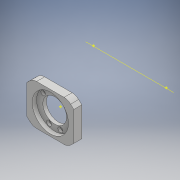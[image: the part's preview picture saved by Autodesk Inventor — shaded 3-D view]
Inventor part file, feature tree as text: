
AUTODESK INVENTOR PART (.ipt)
format: ipt  version: 2018 (Build 220112000, 112)  size: 751,616 bytes
history: native  units: mm
features: sketch x38, projected_geometry x38, extrude x32, other x10, chamfer x7, fillet x5, hole x4, reference x3, mirror x1, plane x1
ambient origin geometry x8: Origin, YZ Plane, XZ Plane, XY Plane, X Axis, Y Axis, Z Axis, Center Point
bodies: Solid1 (feature_tree)
feature tree (139):
  extrude  "Extrusion1"  Depth=45.0mm
  extrude  "Extrusion2"  Depth=2.25mm
  hole  "Hole1"  [1 undecoded]
  hole  "Hole2"  [1 undecoded]
  fillet  "Fillet1"  Radius=14.0mm
  extrude  "Extrusion3"  Depth=18.5mm
  extrude  "Extrusion4"  Depth=10.0mm
  extrude  "Extrusion5"  Depth=2.0mm
  extrude  "Extrusion6"  Depth=2.0mm
  hole  "Hole3"  [1 undecoded]
  extrude  "Extrusion7"  Depth=2.0mm
  extrude  "Extrusion8"  Depth=1.0mm TaperAngle=0.0deg
  extrude  "Extrusion9"  Depth=24.5mm
  extrude  "Extrusion10"  Depth=10.0mm
  extrude  "Extrusion11"  Depth=14.5mm
  extrude  "Extrusion13"  Depth=14.5mm
  extrude  "Extrusion14"  Depth=5.0mm
  extrude  "Extrusion15"  Depth=2.25mm
  extrude  "Extrusion16"  Depth=5.0mm
  extrude  "Extrusion17"  Depth=9.0mm
  chamfer  "Chamfer1"  Distance=1.0mm
  fillet  "Fillet7"  Radius=20.7mm
  fillet  "Fillet8"  Radius=32.0mm
  mirror  "Mirror1"
  sketch  "Sketch26"  dims[d55=2.25mm d56=5.0mm]
  extrude  "Extrusion24"  Depth=1.0mm TaperAngle=0.0deg
  extrude  "Extrusion25"  Depth=8.0mm
  extrude  "Extrusion26"  Depth=0.2mm TaperAngle=0.0deg
  extrude  "Extrusion27"  Depth=5.0mm TaperAngle=0.0deg
  other  "Work Axis1"
  plane  "Work Plane2"
  extrude  "Extrusion28"  Depth=0.2mm TaperAngle=0.0deg
  extrude  "Extrusion29"  Depth=2.0mm TaperAngle=45.0deg
  chamfer  "Chamfer2"  Distance=15.0mm
  extrude  "Extrusion31"  Depth=2.2mm TaperAngle=0.0deg
  chamfer  "Chamfer3"  Distance=15.0mm
  chamfer  "Chamfer4"  Distance=15.0mm
  extrude  "Extrusion32"  Depth=2.2mm
  chamfer  "Chamfer5"  Distance=41.5mm
  extrude  "Extrusion33"  Depth=2.2mm
  sketch  "Sketch41"  dims[d100=0.2mm d101=0.0mm d102=2.5mm d103=2.0mm d104=45.0deg]
  extrude  "Extrusion34"  Depth=2.2mm
  chamfer  "Chamfer6"  Distance=7.0mm
  fillet  "Fillet9"  Radius=100.0mm
  extrude  "Extrusion35"  Depth=2.2mm TaperAngle=0.0deg
  extrude  "Extrusion36"  Depth=2.0mm TaperAngle=45.0deg
  chamfer  "Chamfer7"  [1 undecoded]
  fillet  "Fillet10"  Radius=11.5mm
  extrude  "Extrusion37"  Depth=2.2mm
  extrude  "Extrusion38"  Depth=2.2mm
  extrude  "Extrusion39"  Depth=2.2mm TaperAngle=0.0deg
  extrude  "Extrusion40"  Depth=2.0mm TaperAngle=45.0deg
  hole  "Hole6"  [1 undecoded]
  sketch  "Sketch1"  dims[d0=24.5mm d1=45.0mm]
  sketch  "Sketch2"  dims[d2=1.95mm d3=0.0mm d4=2.25mm]
  projected_geometry  "Projected Loop1"
  sketch  "Sketch3"  dims[d5=20.0mm d6=2.25mm]
  projected_geometry  "Projected Loop2"
  sketch  "Sketch4"  dims[d7=5.25mm d8=5.25mm d9=14.0mm]
  projected_geometry  "Projected Loop3"
  sketch  "Sketch5"  dims[d10=5.25mm d11=18.5mm]
  projected_geometry  "Projected Loop4"
  sketch  "Sketch6"  dims[d12=10.0mm d13=0.0mm d14=20.5mm]
  projected_geometry  "Projected Loop5"
  sketch  "Sketch7"  dims[d15=2.0mm d16=2.195mm]
  projected_geometry  "Projected Loop6"
  sketch  "Sketch8"  dims[d17=2.0mm]
  projected_geometry  "Projected Loop7"
  sketch  "Sketch9"  dims[d18=2.4mm d19=6.0mm d20=4.4mm d21=2.0mm d22=90.0deg d23=8.0mm d24=20.594885mm d25=20.5mm]
  projected_geometry  "Projected Loop8"
  projected_geometry  "Projected Loop9"
  sketch  "Sketch10"  dims[d26=26.65mm d27=2.0mm]
  projected_geometry  "Projected Loop10"
  projected_geometry  "Projected Loop11"
  sketch  "Sketch11"  dims[d28=2.0mm]
  projected_geometry  "Projected Loop12"
  sketch  "Sketch12"  dims[d29=2.4mm d30=6.0mm d31=4.4mm d32=2.0mm d33=90.0deg d34=8.0mm d35=20.594885mm d36=0.5mm]
  sketch  "Sketch13"  dims[d37=18.0mm d38=1.0mm d39=0.0mm]
  sketch  "Sketch14"  dims[d41=5.0mm d42=0.0mm d43=24.5mm]
  projected_geometry  "Projected Loop13"
  sketch  "Sketch16"  dims[d44=1.15mm d45=0.0mm d46=10.0mm]
  projected_geometry  "Projected Loop14"
  sketch  "Sketch17"  dims[d47=21.0mm d48=14.5mm]
  projected_geometry  "Projected Loop15"
  sketch  "Sketch18"  dims[d49=20.0mm d50=14.5mm]
  projected_geometry  "Projected Loop16"
  sketch  "Sketch19"  dims[d51=24.5mm d52=5.0mm]
  projected_geometry  "Projected Loop17"
  sketch  "Sketch20"  dims[d53=5.0mm d54=2.25mm]
  projected_geometry  "Projected Loop18"
  projected_geometry  "Projected Loop25"
  sketch  "Sketch31"  dims[d57=5.0mm d58=9.0mm]
  projected_geometry  "Projected Loop30"
  reference  "Reference1"
  sketch  "Sketch32"  dims[d59=14.75mm]
  projected_geometry  "Projected Loop31"
  sketch  "Sketch33"  dims[d60=4.0mm d61=1.0mm d62=0.0mm d63=20.7mm]
  projected_geometry  "Projected Loop32"
  sketch  "Sketch34"  dims[d64=2.4mm d65=6.0mm d66=4.4mm d67=2.0mm d68=90.0deg d69=8.0mm d70=20.594885mm d72=32.0mm]
  projected_geometry  "Projected Loop33"
  other  "Work Point1"
  other  "Work Point2"
  other  "Work Point3"
  sketch  "Sketch35"  dims[d73=3.0mm d74=0.0mm d75=1.0mm d76=0.0mm]
  sketch  "Sketch37"  dims[d77=12.25mm d78=0.0mm d80=8.0mm]
  projected_geometry  "Projected Loop34"
  sketch  "Sketch38"  dims[d81=4.5mm d82=0.0mm d84=0.2mm d85=0.0mm]
  sketch  "Sketch39"  dims[d91=8.0mm d92=0.0mm d93=5.0mm d94=0.0mm]
  sketch  "Sketch40"  dims[d95=5.0mm d96=0.0mm d98=0.2mm d99=0.0mm]
  projected_geometry  "Projected Loop35"
  projected_geometry  "Projected Loop36"
  projected_geometry  "Projected Loop37"
  projected_geometry  "Projected Loop38"
  sketch  "Sketch42"  dims[d105=1.5mm]
  projected_geometry  "Projected Loop39"
  sketch  "Sketch43"  dims[d114=0.5mm]
  reference  "Reference2"
  reference  "Reference3"
  sketch  "Sketch45"  dims[d130=60.0mm]
  projected_geometry  "Projected Loop40"
  sketch  "Sketch46"  dims[d131=36.0mm]
  projected_geometry  "Projected Loop41"
  sketch  "Sketch48"  dims[d146=40.0mm]
  projected_geometry  "Projected Loop43"
  sketch  "Sketch49"  dims[d147=60.0mm]
  projected_geometry  "Projected Loop44"
  projected_geometry  "Projected Loop45"
  sketch  "Sketch50"  dims[d148=0.0mm]
  projected_geometry  "Projected Loop46"
  sketch  "Sketch52"  dims[d149=2.3mm d150=15.0mm d151=0.0mm d152=15.0mm d153=0.0mm d154=15.0mm d155=0.0mm d156=15.0mm d157=0.0mm d158=20.5mm d159=41.5mm d160=14.0mm d161=14.0mm d162=7.0mm d165=100.0mm d166=0.0mm d167=100.0mm d168=0.0mm d169=6.0mm d170=2.0mm d171=45.0deg d172=0.0mm d173=11.5mm d175=11.5mm d176=11.5mm d179=100.0mm d180=0.0mm d181=5.0mm d182=2.0mm d183=45.0deg d184=5.0mm d185=2.0mm d186=45.0deg d187=8.0mm d188=100.0mm d189=0.0mm d190=5.0mm d191=2.0mm d192=45.0deg d193=100.0mm d194=0.0mm d195=100.0mm d196=0.0mm d197=5.0mm d198=2.0mm d199=45.0deg d200=8.0mm d202=15.0deg d204=10.970628mm d205=15.470628mm d206=2.5mm d207=0.0mm d208=2.5mm d209=0.0mm d210=3.0mm d211=2.0mm d212=45.0deg d213=2.0mm d215=15.0deg d216=4.0mm d217=4.0mm d218=5.0mm d219=0.0mm d222=32.07mm d223=3.9mm d224=0.0mm d225=2.8mm d226=0.0mm d227=7.1mm d228=0.0mm d229=5.0mm d230=2.2mm d231=6.0mm d232=4.4mm d233=2.2mm d234=90.0deg d235=8.0mm d236=20.594885mm]
  projected_geometry  "Projected Loop47"
  parser-record x1  (decoder bookkeeping rows leaked as tree rows — omitted from the tree; the rows remain in map.json)
  other  "servocheck.iam"
  other  "LX-16A:3"
  other  "DUOPAN-SG-SJ_10"
  projected_geometry  "Project Cut Edges1"
  projected_geometry  "Project Cut Edges3"
  other  "bottomarm:1"
  other  "arm1:1"
note: 5 required parameter values undecoded (feature->parameter linkage not recoverable at this tier; creation-order binding heuristic only, values carry confidence <= 0.55)
note: 1 file-system path scrubbed to <path> (originals preserved in map.json)
